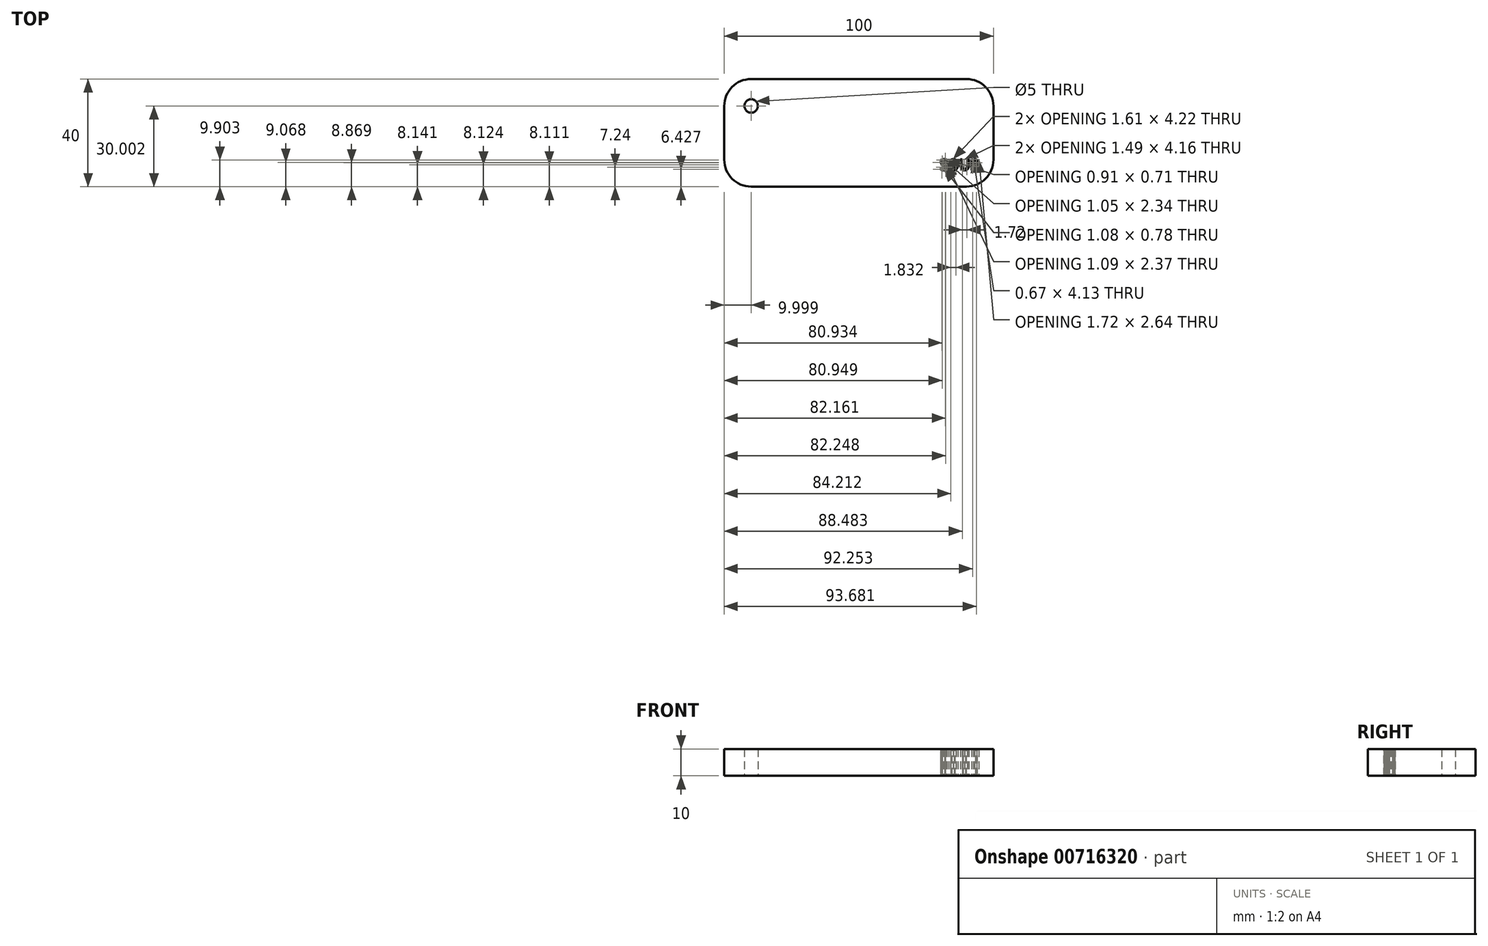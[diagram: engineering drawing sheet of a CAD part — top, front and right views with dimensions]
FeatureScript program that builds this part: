
annotation { "Feature Type Name" : "Feature", "Feature Type Description" : "" }
export const myFeature = defineFeature(function(context is Context, id is Id, definition is map)
    precondition{}
    {
        {
            var Q0;
            Q0=qCreatedBy(makeId("Top.planeOp"),FACE);
            var sketch = newSketch(context, id + "F0", { "sketchPlane" : qUnion([Q0])});
            skLineSegment(sketch, "E0.bottom", {"start": v(-37.75, 18.14) * mm, "end": v(42.25, 18.14) * mm});
            skLineSegment(sketch, "E0.top", {"start": v(-37.75, -21.86) * mm, "end": v(42.25, -21.86) * mm});
            skLineSegment(sketch, "E0.left", {"start": v(-47.75, 8.14) * mm, "end": v(-47.75, -11.86) * mm});
            skLineSegment(sketch, "E0.right", {"start": v(52.25, 8.14) * mm, "end": v(52.25, -11.86) * mm});
            skPoint(sketch, "E1.visualSharp", {"position": v(-47.75, 18.14) * mm});
            skArc(sketch, "E1.filletArc", {"start": v(-37.75, 18.14) * mm, "mid": v(-44.82, 15.21) * mm, "end": v(-47.75, 8.14) * mm});
            skPoint(sketch, "E2.visualSharp", {"position": v(52.25, 18.14) * mm});
            skArc(sketch, "E2.filletArc", {"start": v(52.25, 8.14) * mm, "mid": v(49.32, 15.21) * mm, "end": v(42.25, 18.14) * mm});
            skPoint(sketch, "E3.visualSharp", {"position": v(-47.75, -21.86) * mm});
            skArc(sketch, "E3.filletArc", {"start": v(-47.75, -11.86) * mm, "mid": v(-44.82, -18.93) * mm, "end": v(-37.75, -21.86) * mm});
            skPoint(sketch, "E4.visualSharp", {"position": v(52.25, -21.86) * mm});
            skArc(sketch, "E4.filletArc", {"start": v(42.25, -21.86) * mm, "mid": v(49.32, -18.93) * mm, "end": v(52.25, -11.86) * mm});
            skCircle(sketch, "E5", {"center": v(-37.75, 8.14) * mm, "radius": 2.5 * mm});
            skText(sketch, "E6", { "text": "SOUP", "fontName": "AllertaStencil-Regular.ttf"});
            const initialGuessF0  = {"E6": [0.03219, -0.0158, 1, 0, 0.00413]};
            skSetInitialGuess(sketch, initialGuessF0);
            skSolve(sketch);
        }
        {
            var Q0;
            Q0 = qSketchRegion(id + "F0", true);
            extrude(context, id + "F1", {"entities" : qUnion([Q0]), "depth" : 10 * mm, "offsetDistance" : 25 * mm});
        }
    });
